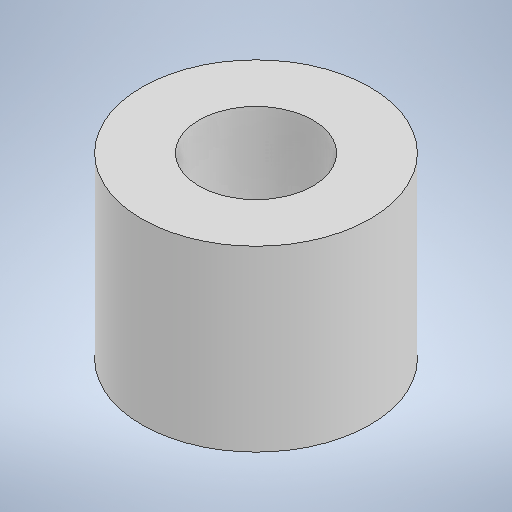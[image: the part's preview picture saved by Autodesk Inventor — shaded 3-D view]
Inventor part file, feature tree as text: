
AUTODESK INVENTOR PART (.ipt)
format: ipt  version: 2025.1 (Build 291241000, 241)  size: 192,512 bytes
history: native  units: mm
features: extrude x1, sketch x1
ambient origin geometry x8: Origin, YZ Plane, XZ Plane, XY Plane, X Axis, Y Axis, Z Axis, Center Point
bodies: Solid1 (feature_tree)
feature tree (2):
  extrude  "Extrusion1"  Depth=8.0mm
  sketch  "Sketch1"  dims[d0=16.0mm d1=8.0mm d2=12.5mm d3=0.0mm]
